FCSTD DOCUMENT  (FreeCAD 0.16R6704 (Git))
Label: calibpattern_v2
License: All rights reserved
LicenseURL: http://en.wikipedia.org/wiki/All_rights_reserved
objects: Sketcher::SketchObject×1, Spreadsheet::Sheet×1, Drawing::FeatureViewPart×1, Drawing::FeaturePage×1
note: 1 computed .brp shape members not serialized (recipe doc carries the construction recipe); baked Part::Feature solids carry a one-line shape summary decoded from their .brp

FEATURE [Sketcher::SketchObject] Sketch
  expr: Constraints[204] = Data.s_small + (Data.s_big - Data.s_small) / 4
  expr: Constraints[203] = Data.s_small + 3 * (Data.s_big - Data.s_small) / 4
  expr: Constraints[200] = Data.s_small + 3 * (Data.s_big - Data.s_small) / 4
  expr: Constraints[198] = Data.s_small + (Data.s_big - Data.s_small) / 4
  expr: Constraints[206] = Data.s_small + 3 * (Data.s_big - Data.s_small) / 4
  expr: Constraints[202] = Data.s_small + 2 * (Data.s_big - Data.s_small) / 4
  expr: Constraints[193] = Data.s_small + 2 * (Data.s_big - Data.s_small) / 4
  expr: Constraints[195] = Data.s_small + (Data.s_big - Data.s_small) / 4
  expr: Constraints[191] = Data.s_small + 3 * (Data.s_big - Data.s_small) / 4
  expr: Constraints[190] = Data.s_small + 2 * (Data.s_big - Data.s_small) / 4
  expr: Constraints[196] = Data.s_small + 2 * (Data.s_big - Data.s_small) / 4
  expr: Constraints[188] = Data.s_small + 3 * (Data.s_big - Data.s_small) / 4
  expr: Constraints[197] = Data.s_small + 3 * (Data.s_big - Data.s_small) / 4
  expr: Constraints[187] = Data.s_small + 2 * (Data.s_big - Data.s_small) / 4
  expr: Constraints[186] = Data.s_small + (Data.s_big - Data.s_small) / 4
  expr: Constraints[25] = 4 * Data.alpha / 6
  expr: Constraints[22] = Data.alpha / 6
  expr: Constraints[194] = Data.s_small + 3 * (Data.s_big - Data.s_small) / 4
  expr: Constraints[6] = Data.s_big
  expr: Constraints[26] = 5 * Data.alpha / 6
  expr: Constraints[189] = Data.s_small + (Data.s_big - Data.s_small) / 4
  expr: Constraints[7] = Data.alpha
  expr: Constraints[192] = Data.s_small + (Data.s_big - Data.s_small) / 4
  expr: Constraints[199] = Data.s_small + 2 * (Data.s_big - Data.s_small) / 4
  expr: Constraints[24] = 3 * Data.alpha / 6
  expr: Constraints[11] = Data.s_small
  expr: Constraints[201] = Data.s_small + (Data.s_big - Data.s_small) / 4
  expr: Constraints[23] = 2 * Data.alpha / 6
  sketch-geometry (65):
    g0: LineSegment StartX=0 StartY=0 StartZ=0 EndX=0 EndY=125.3 EndZ=0
    g1: ArcOfCircle CenterX=0 CenterY=0 CenterZ=0 NormalX=0 NormalY=0 NormalZ=1 Radius=125.3 StartAngle=1.5708 EndAngle=4.57951
    g2: LineSegment StartX=0 StartY=0 StartZ=0 EndX=-16.6004 EndY=-124.195 EndZ=0
    g3: ArcOfCircle CenterX=0 CenterY=0 CenterZ=0 NormalX=0 NormalY=0 NormalZ=1 Radius=27.1483 StartAngle=1.5708 EndAngle=4.57951
    g4: LineSegment StartX=0 StartY=0 StartZ=0 EndX=-74.2572 EndY=-100.925 EndZ=0
    g5: LineSegment StartX=0 StartY=0 StartZ=0 EndX=-113.63 EndY=-52.8043 EndZ=0
    g6: LineSegment StartX=0 StartY=0 StartZ=0 EndX=-125.023 EndY=8.31853 EndZ=0
    g7: LineSegment StartX=0 StartY=0 StartZ=0 EndX=-105.632 EndY=67.393 EndZ=0
    g8: LineSegment StartX=0 StartY=0 StartZ=0 EndX=-60.2315 EndY=109.873 EndZ=0
    g9: Circle CenterX=0 CenterY=27.1483 CenterZ=0 NormalX=0 NormalY=0 NormalZ=1 Radius=5
    g10: Circle CenterX=0 CenterY=125.3 CenterZ=0 NormalX=0 NormalY=0 NormalZ=1 Radius=5
    g11: Circle CenterX=-60.2315 CenterY=109.873 CenterZ=0 NormalX=0 NormalY=0 NormalZ=1 Radius=5
    g12: Circle CenterX=-105.632 CenterY=67.393 CenterZ=0 NormalX=0 NormalY=0 NormalZ=1 Radius=5
    g13: Circle CenterX=-125.023 CenterY=8.31853 CenterZ=0 NormalX=0 NormalY=0 NormalZ=1 Radius=5
    g14: Circle CenterX=-13.0502 CenterY=23.8059 CenterZ=0 NormalX=0 NormalY=0 NormalZ=1 Radius=5
    g15: Circle CenterX=-22.887 CenterY=14.6018 CenterZ=0 NormalX=0 NormalY=0 NormalZ=1 Radius=5
    g16: Circle CenterX=-27.0884 CenterY=1.80235 CenterZ=0 NormalX=0 NormalY=0 NormalZ=1 Radius=5
    g17: Circle CenterX=-24.6198 CenterY=-11.4409 CenterZ=0 NormalX=0 NormalY=0 NormalZ=1 Radius=5
    g18: Circle CenterX=-16.0891 CenterY=-21.8671 CenterZ=0 NormalX=0 NormalY=0 NormalZ=1 Radius=5
    g19: Circle CenterX=-3.59675 CenterY=-26.9089 CenterZ=0 NormalX=0 NormalY=0 NormalZ=1 Radius=5
    g20: Circle CenterX=-113.63 CenterY=-52.8043 CenterZ=0 NormalX=0 NormalY=0 NormalZ=1 Radius=5
    g21: Circle CenterX=-74.2572 CenterY=-100.925 CenterZ=0 NormalX=0 NormalY=0 NormalZ=1 Radius=5
    g22: Circle CenterX=-16.6004 CenterY=-124.195 CenterZ=0 NormalX=0 NormalY=0 NormalZ=1 Radius=5
    g23: LineSegment StartX=-79.5674 StartY=62.6256 StartZ=0 EndX=-84.946 EndY=54.1952 EndZ=0
    g24: LineSegment StartX=-90.3245 StartY=45.7649 StartZ=0 EndX=-84.946 EndY=54.1952 EndZ=0
    g25: LineSegment StartX=-58.8811 StartY=49.4278 StartZ=0 EndX=-64.2596 EndY=40.9974 EndZ=0
    g26: LineSegment StartX=-69.6382 StartY=32.5671 StartZ=0 EndX=-64.2596 EndY=40.9974 EndZ=0
    g27: LineSegment StartX=-38.1948 StartY=36.23 StartZ=0 EndX=-43.5733 EndY=27.7996 EndZ=0
    g28: LineSegment StartX=-100.539 StartY=6.68949 StartZ=0 EndX=-99.8756 EndY=16.6674 EndZ=0
    g29: LineSegment StartX=-100.539 StartY=6.68949 StartZ=0 EndX=-101.203 EndY=-3.28845 EndZ=0
    g30: LineSegment StartX=-76.0558 StartY=5.06044 StartZ=0 EndX=-75.3919 EndY=15.0384 EndZ=0
    g31: LineSegment StartX=-76.0558 StartY=5.06044 StartZ=0 EndX=-76.7197 EndY=-4.9175 EndZ=0
    g32: LineSegment StartX=-51.5721 StartY=3.4314 StartZ=0 EndX=-50.9082 EndY=13.4093 EndZ=0
    g33: LineSegment StartX=-51.5721 StartY=3.4314 StartZ=0 EndX=-52.236 EndY=-6.54654 EndZ=0
    g34: LineSegment StartX=-48.4362 StartY=88.3565 StartZ=0 EndX=-39.6673 EndY=93.1635 EndZ=0
    g35: LineSegment StartX=-48.4362 StartY=88.3565 StartZ=0 EndX=-57.205 EndY=83.5495 EndZ=0
    g36: LineSegment StartX=-36.6408 StartY=66.8396 StartZ=0 EndX=-27.872 EndY=71.6466 EndZ=0
    g37: LineSegment StartX=-36.6408 StartY=66.8396 StartZ=0 EndX=-45.4097 EndY=62.0326 EndZ=0
    g38: LineSegment StartX=-24.8455 StartY=45.3228 StartZ=0 EndX=-16.0767 EndY=50.1298 EndZ=0
    g39: LineSegment StartX=-24.8455 StartY=45.3228 StartZ=0 EndX=-33.6144 EndY=40.5158 EndZ=0
    g40: LineSegment StartX=0 StartY=100.762 StartZ=0 EndX=10 EndY=100.762 EndZ=0
    g41: LineSegment StartX=0 StartY=100.762 StartZ=0 EndX=-10 EndY=100.762 EndZ=0
    g42: LineSegment StartX=0 StartY=76.2239 StartZ=0 EndX=10 EndY=76.2239 EndZ=0
    g43: LineSegment StartX=0 StartY=76.2239 StartZ=0 EndX=-10 EndY=76.2239 EndZ=0
    g44: LineSegment StartX=0 StartY=51.6861 StartZ=0 EndX=10 EndY=51.6861 EndZ=0
    g45: LineSegment StartX=0 StartY=51.6861 StartZ=0 EndX=-10 EndY=51.6861 EndZ=0
    g46: LineSegment StartX=-91.3772 StartY=-42.4634 StartZ=0 EndX=-87.163 EndY=-51.5321 EndZ=0
    g47: LineSegment StartX=-91.3772 StartY=-42.4634 StartZ=0 EndX=-95.5915 EndY=-33.3948 EndZ=0
    g48: LineSegment StartX=-69.1247 StartY=-32.1226 StartZ=0 EndX=-64.9105 EndY=-41.1912 EndZ=0
    g49: LineSegment StartX=-69.1247 StartY=-32.1226 StartZ=0 EndX=-73.339 EndY=-23.0539 EndZ=0
    g50: LineSegment StartX=-46.8723 StartY=-21.7818 StartZ=0 EndX=-42.658 EndY=-30.8504 EndZ=0
    g51: LineSegment StartX=-46.8723 StartY=-21.7818 StartZ=0 EndX=-51.0865 EndY=-12.7131 EndZ=0
    g52: LineSegment StartX=-30.6311 StartY=-41.6316 StartZ=0 EndX=-22.5764 EndY=-47.558 EndZ=0
    g53: LineSegment StartX=-30.6311 StartY=-41.6316 StartZ=0 EndX=-38.6858 EndY=-35.7052 EndZ=0
    g54: LineSegment StartX=-45.1731 StartY=-61.3961 StartZ=0 EndX=-37.1184 EndY=-67.3224 EndZ=0
    g55: LineSegment StartX=-45.1731 StartY=-61.3961 StartZ=0 EndX=-53.2278 EndY=-55.4697 EndZ=0
    g56: LineSegment StartX=-59.7152 StartY=-81.1606 StartZ=0 EndX=-51.6605 EndY=-87.0869 EndZ=0
    g57: LineSegment StartX=-59.7152 StartY=-81.1606 StartZ=0 EndX=-67.7699 EndY=-75.2342 EndZ=0
    g58: LineSegment StartX=-6.84765 StartY=-51.2305 StartZ=0 EndX=3.0642 EndY=-52.5553 EndZ=0
    g59: LineSegment StartX=-6.84765 StartY=-51.2305 StartZ=0 EndX=-16.7595 EndY=-49.9056 EndZ=0
    g60: LineSegment StartX=-9.57984 StartY=-71.6713 StartZ=0 EndX=0.332009 EndY=-72.9961 EndZ=0
    g61: LineSegment StartX=-9.57984 StartY=-71.6713 StartZ=0 EndX=-19.4917 EndY=-70.3464 EndZ=0
    g62: LineSegment StartX=-13.3495 StartY=-99.8736 StartZ=0 EndX=-3.43761 EndY=-101.198 EndZ=0
    g63: LineSegment StartX=-13.3495 StartY=-99.8736 StartZ=0 EndX=-23.2613 EndY=-98.5487 EndZ=0
    g64: LineSegment StartX=-43.5733 StartY=27.7996 StartZ=0 EndX=-48.9519 EndY=19.3693 EndZ=0
  constraints (207):
    c: Coincident(g0,g-1)
    c: PointOnObject(g0,g-2)
    c: Coincident(g1,g-1)
    c: Coincident(g1,g0)
    c: Coincident(g2,g-1)
    c: Coincident(g2,g1)
    c: Distance(g0) = 125.3
    c: Angle(g1) = 3.00872
    c: Coincident(g3,g-1)
    c: PointOnObject(g3,g0)
    c: PointOnObject(g3,g2)
    c: Radius(g3) = 27.1483
    c: Coincident(g4,g-1)
    c: Coincident(g5,g-1)
    c: PointOnObject(g5,g1)
    c: Coincident(g6,g-1)
    c: Coincident(g7,g-1)
    c: PointOnObject(g7,g1)
    c: PointOnObject(g8,g1)
    c: Coincident(g8,g-1)
    c: PointOnObject(g4,g1)
    c: PointOnObject(g6,g1)
    c: Angle(g4,g2) = 0.501453
    c: Angle(g5,g2) = 1.00291
    c: Angle(g6,g2) = 1.50436
    c: Angle(g7,g2) = 2.00581
    c: Angle(g8,g2) = 2.50726
    c: Coincident(g9,g3)
    c: Coincident(g10,g0)
    c: Coincident(g11,g8)
    c: Coincident(g12,g7)
    c: Coincident(g13,g6)
    c: PointOnObject(g14,g3)
    c: PointOnObject(g15,g3)
    c: PointOnObject(g16,g6)
    c: PointOnObject(g17,g5)
    c: PointOnObject(g18,g4)
    c: Coincident(g19,g3)
    c: PointOnObject(g15,g7)
    c: PointOnObject(g14,g8)
    c: PointOnObject(g18,g3)
    c: PointOnObject(g16,g3)
    c: PointOnObject(g17,g3)
    c: Coincident(g20,g5)
    c: Coincident(g21,g4)
    c: Coincident(g22,g1)
    c: Equal(g10,g11)
    c: Equal(g11,g12)
    c: Equal(g12,g13)
    c: Equal(g13,g20)
    c: Equal(g20,g21)
    c: Equal(g21,g22)
    c: Equal(g22,g19)
    c: Equal(g19,g18)
    c: Equal(g18,g17)
    c: Equal(g17,g16)
    c: Equal(g16,g15)
    c: Equal(g15,g14)
    c: Equal(g14,g9)
    c: PointOnObject(g23,g7)
    c: Coincident(g24,g23)
    c: PointOnObject(g25,g7)
    c: Coincident(g26,g25)
    c: PointOnObject(g27,g7)
    c: PointOnObject(g28,g6)
    c: Coincident(g29,g28)
    c: PointOnObject(g30,g6)
    c: Coincident(g31,g30)
    c: PointOnObject(g32,g6)
    c: Coincident(g33,g32)
    c: PointOnObject(g34,g8)
    c: Coincident(g35,g34)
    c: PointOnObject(g36,g8)
    c: Coincident(g37,g36)
    c: PointOnObject(g38,g8)
    c: Coincident(g39,g38)
    c: PointOnObject(g40,g0)
    c: Coincident(g41,g40)
    c: PointOnObject(g42,g0)
    c: Coincident(g43,g42)
    c: PointOnObject(g44,g0)
    c: Coincident(g45,g44)
    c: PointOnObject(g46,g5)
    c: Coincident(g47,g46)
    c: PointOnObject(g48,g5)
    c: Coincident(g49,g48)
    c: PointOnObject(g50,g5)
    c: Coincident(g51,g50)
    c: PointOnObject(g52,g4)
    c: Coincident(g53,g52)
    c: PointOnObject(g54,g4)
    c: Coincident(g55,g54)
    c: PointOnObject(g56,g4)
    c: Coincident(g57,g56)
    c: PointOnObject(g58,g2)
    c: Coincident(g59,g58)
    c: PointOnObject(g60,g2)
    c: Coincident(g61,g60)
    c: PointOnObject(g62,g2)
    c: Coincident(g63,g62)
    c: Equal(g40,g41)
    c: Equal(g41,g43)
    c: Equal(g43,g42)
    c: Equal(g42,g44)
    c: Equal(g44,g45)
    c: Equal(g34,g41)
    c: Equal(g41,g36)
    c: Equal(g36,g38)
    c: Equal(g38,g37)
    c: Equal(g37,g35)
    c: Equal(g35,g39)
    c: Coincident(g64,g27)
    c: Equal(g26,g24)
    c: Equal(g24,g23)
    c: Equal(g23,g25)
    c: Equal(g25,g64)
    c: Equal(g64,g27)
    c: Equal(g27,g34)
    c: Equal(g32,g30)
    c: Equal(g30,g28)
    c: Equal(g28,g29)
    c: Equal(g29,g31)
    c: Equal(g31,g33)
    c: Equal(g33,g24)
    c: Equal(g51,g49)
    c: Equal(g49,g47)
    c: Equal(g47,g46)
    c: Equal(g46,g48)
    c: Equal(g48,g50)
    c: Equal(g50,g32)
    c: Equal(g52,g53)
    c: Equal(g53,g54)
    c: Equal(g54,g55)
    c: Equal(g55,g57)
    c: Equal(g57,g56)
    c: Equal(g56,g46)
    c: Equal(g58,g59)
    c: Equal(g59,g61)
    c: Equal(g61,g60)
    c: Equal(g60,g62)
    c: Equal(g62,g63)
    c: Equal(g63,g56)
    c: Distance(g58) = 10
    c: Angle(g59,g58) = 3.14159
    c: Angle(g2,g59) = 1.5708
    c: Angle(g60,g61) = 3.14159
    c: Angle(g2,g61) = 1.5708
    c: Angle(g63,g62) = 3.14159
    c: Angle(g2,g63) = 1.5708
    c: Angle(g53,g52) = 3.14159
    c: Angle(g4,g53) = 1.5708
    c: Angle(g55,g54) = 3.14159
    c: Angle(g4,g55) = 1.5708
    c: Angle(g57,g56) = 3.14159
    c: Angle(g57,g4) = 1.5708
    c: Angle(g50,g51) = 3.14159
    c: Angle(g48,g49) = 3.14159
    c: Angle(g47,g46) = 3.14159
    c: Angle(g47,g5) = 1.5708
    c: Angle(g49,g5) = 1.5708
    c: Angle(g5,g51) = 1.5708
    c: Angle(g33,g32) = 3.14159
    c: Angle(g31,g30) = 3.14159
    c: Angle(g29,g28) = 3.14159
    c: Angle(g6,g28) = 1.5708
    c: Angle(g27,g64) = 3.14159
    c: Angle(g26,g25) = 3.14159
    c: Angle(g24,g23) = 3.14159
    c: Angle(g7,g23) = 1.5708
    c: Angle(g7,g25) = 1.5708
    c: Angle(g7,g27) = 1.5708
    c: Angle(g6,g30) = 1.5708
    c: Angle(g6,g32) = 1.5708
    c: Angle(g38,g39) = 3.14159
    c: Angle(g37,g36) = 3.14159
    c: Angle(g35,g34) = 3.14159
    c: Angle(g34,g8) = 1.5708
    c: Angle(g36,g8) = 1.5708
    c: Angle(g38,g8) = 1.5708
    c: Angle(g40,g41) = 3.14159
    c: Angle(g42,g43) = 3.14159
    c: Angle(g44,g45) = 3.14159
    c: Angle(g0,g44) = 1.5708
    c: Angle(g42,g0) = 1.5708
    c: Angle(g0,g40) = 1.5708
    c: Radius(g9) = 5
    c: Distance(g-1,g45) = 51.6861
    c: Distance(g-1,g42) = 76.2239
    c: Distance(g-1,g40) = 100.762
    c: Distance(g-1,g38) = 51.6861
    c: Distance(g-1,g36) = 76.2239
    c: Distance(g-1,g34) = 100.762
    c: Distance(g-1,g27) = 51.6861
    c: Distance(g-1,g25) = 76.2239
    c: Distance(g-1,g23) = 100.762
    c: Distance(g-1,g32) = 51.6861
    c: Distance(g-1,g30) = 76.2239
    c: Distance(g-1,g28) = 100.762
    c: Distance(g-1,g51) = 51.6861
    c: Distance(g-1,g49) = 76.2239
    c: Distance(g-1,g47) = 100.762
    c: Distance(g-1,g52) = 51.6861
    c: Distance(g-1,g54) = 76.2239
    c: Distance(g-1,g57) = 100.762
    c: Distance(g-1,g58) = 51.6861
    c: Distance(g-1,g60) = 72.3087
    c: Distance(g-1,g62) = 100.762
FEATURE [Spreadsheet::Sheet] Spreadsheet  label="Data"
  cells = A1=R; B1(r_big)=60; A2=r; B2(r_small)=13; A3=H; B3(h_big)=110; A9=calculated:; A10=S; B10(s_big)==sqrt(h_big * h_big + r_big * r_big); C10=whole cone outer; A11=alpha; B11(alpha)==360 * r_big / s_big; A12=h; B12(h_small)==h_big * r_small / r_big; C12=top cone outer; A13=s; B13(s_small)==sqrt(h_small * h_small + r_small * r_small); C13=top cone outer
FEATURE [Drawing::FeatureViewPart] Ortho  label="Draft"
  Direction = (0,0,1)
  HiddenWidth = 0.15
  LineWidth = 20.35
  Rotation = 0
  ShowHiddenLines = false
  ShowSmoothLines = false
  Source = -> Sketch
  Tolerance = 0.05
  ViewResult = <g id="Ortho_0_0"\n   transform="rotate(0,167.512,149.052) translate(167.512,149.052) scale(1,1)"\n  >\n<g   stroke="rgb(0, 0, 0)"\n   stroke-width="0.35"\n   stroke-linecap="butt"\n   stroke-linejoin="miter"\n   fill="none"\n   transform="scale(1,-1)"\n  >\n<path id= "1" d=" M 0 0 L -60.2315 109.873 " />\n<path id= "2" d=" M 0 0 L -105.632 67.393 " />\n<path id= "3" d=" M 0 0 L -125.023 8.31853 " />\n<path id= "4" d=" M 0 0 L -113.63 -52.8043 " />\n<path id= "5" d=" M 0 0 L 0 125.3 " />\n<path d="M7.67239e-15 125.3 A125.3 125.3 0 0 1 -16.6004 -124.195" /><path id= "7" d=" M 0 0 L -16.6004 -124.195 " />\n<path id= "8" d=" M 0 0 L -74.2572 -100.925 " />\n<path d="M1.66235e-15 27.1483 A27.1483 27.1483 0 0 1 -3.59675 -26.9089" /><path d="M4.66737e-15 76.2239 A76.2239 76.2239 0 0 1 -10.0986 -75.552" /><path d="M6.16988e-15 100.762 A100.762 100.762 0 0 1 -13.3495 -99.8736" /><path d="M3.16486e-15 51.6861 A51.6861 51.6861 0 0 1 -6.84765 -51.2305" /></g>\n</g>
  Visible = true
  X = 167.512
  Y = 149.052
FEATURE [Drawing::FeaturePage] Page
  Group = -> [Ortho]
